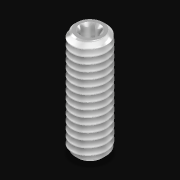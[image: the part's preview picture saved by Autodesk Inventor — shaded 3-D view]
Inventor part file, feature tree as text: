
AUTODESK INVENTOR PART (.ipt)
format: ipt  version: 2021 (Build 250183000, 183)  size: 754,176 bytes
history: native  units: in
note: dims shown in document units (in); Inventor stores cm internally (conversion verified against a paired STEP export)
features: other x10, sketch x10, extrude x3, thread x1
ambient origin geometry x8: Origin, YZ Plane, XZ Plane, XY Plane, X Axis, Y Axis, Z Axis, Center Point
bodies: Solid1 (feature_tree), Body (feature_tree)
feature tree (24):
  other  "Table"
  other  "Coupler Star .5"
  other  "Coupler Star 1"
  other  "Coupler Hex .5"
  other  "Coupler Hex 1"
  thread  "Thread"  [1 undecoded]
  other  "Tapered End"
  extrude  "Flatten Threads"  TaperAngle=60.0deg  [1 undecoded]
  extrude  "Hex"  Depth=0.0312in
  other  "Hex Divot"
  other  "Star"
  extrude  "Star 2"  TaperAngle=135.0deg  [1 undecoded]
  other  "Star 3"
  other  "Tapered Head"
  sketch  "Sketch1"  dims[d4=0.123in d32=60.0deg]
  sketch  "Sketch5"  dims[d37=0.0312in d38=0.55in d39=11.811in d40=0.0in d41=90.0deg d42=90.0deg d43=0.0in d44=0.0in d46=0.0312in]
  sketch  "Sketch6"  dims[d49=0.0585in d50=135.0deg]
  sketch  "Sketch7"  dims[d53=90.0deg]
  sketch  "Sketch8"  dims[d54=0.0027in]
  sketch  "Sketch9"  dims[d55=0.0205in]
  sketch  "Sketch10"  dims[d56=0.0039in]
  sketch  "Sketch11"  dims[d57=30.0deg]
  sketch  "Sketch12"  dims[d58=0.5in d59=0.0in]
  sketch  "Sketch13"  dims[d60=0.094in d63=0.044in d64=0.0in d67=360.0deg d70=0.1378in d71=0.047in d73=0.059in d74=90.0deg d75=0.5in d76=0.012in d77=0.082in d78=0.052in d79=0.012in d80=0.012in d81=0.012in d82=0.012in d83=0.012in d84=0.052in d85=0.052in d86=0.052in d87=0.052in d88=0.052in d89=0.25in d90=0.0in d91=45.0deg d92=90.0deg d93=0.5in d94=0.0in d95=0.047in d104=0.015in d105=0.022in d106=0.047in d107=0.0in d108=0.456in d109=45.0deg d110=0.0in d111=0.062in d112=0.5in d113=90.0deg]
note: 3 required parameter values undecoded (feature->parameter linkage not recoverable at this tier; creation-order binding heuristic only, values carry confidence <= 0.55)
